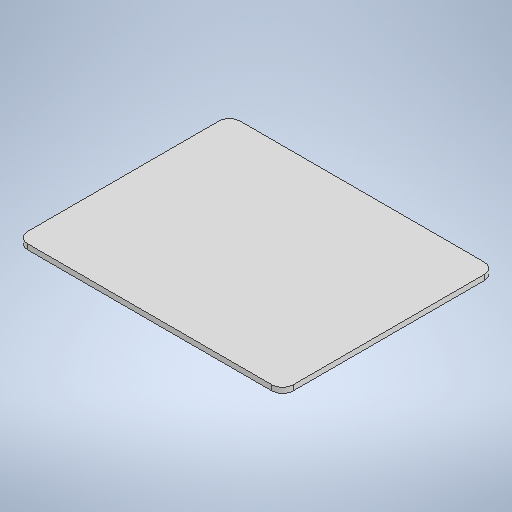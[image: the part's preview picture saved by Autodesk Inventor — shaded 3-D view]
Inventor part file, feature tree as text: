
AUTODESK INVENTOR PART (.ipt)
format: ipt  version: 2025.1 (Build 291241020, 241B)  size: 222,208 bytes
history: native  units: in
note: dims shown in document units (in); Inventor stores cm internally (conversion verified against a paired STEP export)
features: sketch x2, extrude x1, fillet x1
ambient origin geometry x8: Origin, YZ Plane, XZ Plane, XY Plane, X Axis, Y Axis, Z Axis, Center Point
bodies: Solid1 (feature_tree)
feature tree (4):
  sketch  "Sketch1"  dims[d0=9.8425in d1=7.874in d2=0.1969in d3=0.0in]
  extrude  "Extrusion1"  Depth=7.874in
  fillet  "Fillet1"  Radius=0.1969in
  sketch  "Sketch2"  dims[d4=0.3937in]
